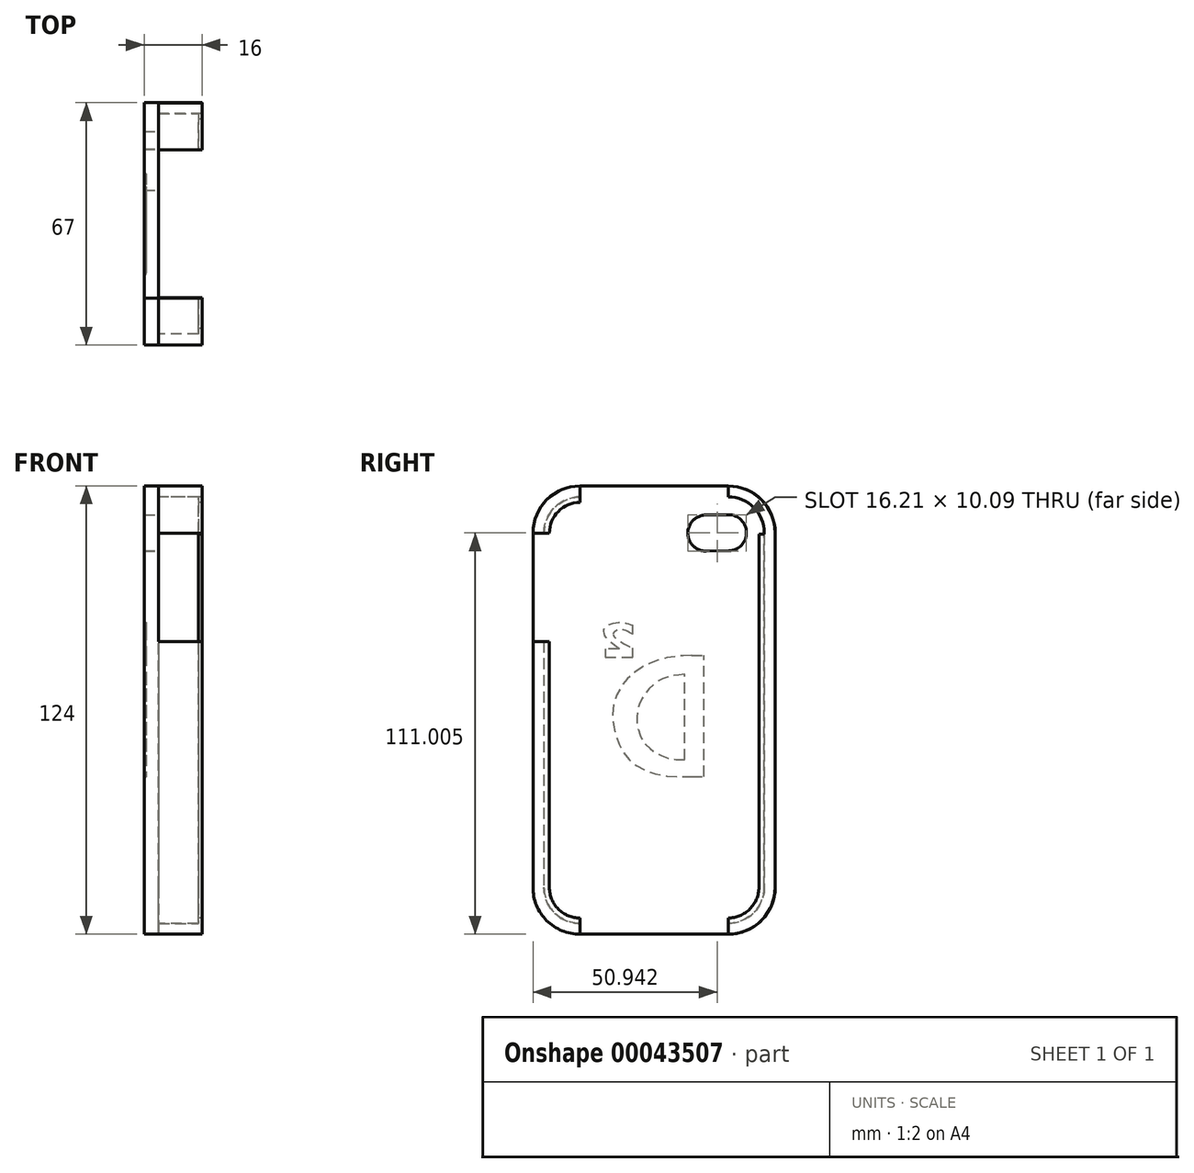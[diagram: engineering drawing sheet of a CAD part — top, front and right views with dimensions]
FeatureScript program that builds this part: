
annotation { "Feature Type Name" : "Feature", "Feature Type Description" : "" }
export const myFeature = defineFeature(function(context is Context, id is Id, definition is map)
    precondition{}
    {
        {
            var Q0;
            Q0=qCreatedBy(makeId("Right.planeOp"),FACE);
            var sketch = newSketch(context, id + "F0", { "sketchPlane" : qUnion([Q0])});
            skLineSegment(sketch, "E0.rect.bottom", {"start": v(20.5, 62) * mm, "end": v(-20.5, 62) * mm});
            skLineSegment(sketch, "E0.rect.top", {"start": v(20.5, -62) * mm, "end": v(-20.5, -62) * mm});
            skLineSegment(sketch, "E0.rect.left", {"start": v(33.5, 49) * mm, "end": v(33.5, -49) * mm});
            skLineSegment(sketch, "E0.rect.right", {"start": v(-33.5, 49) * mm, "end": v(-33.5, -49) * mm});
            skPoint(sketch, "E0.rect.middle", {"position": v(0, 0) * mm});
            skPoint(sketch, "E1.visualSharp", {"position": v(-33.5, 62) * mm});
            skArc(sketch, "E1.filletArc", {"start": v(-20.5, 62) * mm, "mid": v(-29.7, 58.2) * mm, "end": v(-33.5, 49) * mm});
            skPoint(sketch, "E2.visualSharp", {"position": v(-33.5, -62) * mm});
            skArc(sketch, "E2.filletArc", {"start": v(-33.5, -49) * mm, "mid": v(-29.7, -58.2) * mm, "end": v(-20.5, -62) * mm});
            skPoint(sketch, "E3.visualSharp", {"position": v(33.5, 62) * mm});
            skArc(sketch, "E3.filletArc", {"start": v(33.5, 49) * mm, "mid": v(29.7, 58.2) * mm, "end": v(20.5, 62) * mm});
            skPoint(sketch, "E4.visualSharp", {"position": v(33.5, -62) * mm});
            skArc(sketch, "E4.filletArc", {"start": v(20.5, -62) * mm, "mid": v(29.7, -58.2) * mm, "end": v(33.5, -49) * mm});
            skSolve(sketch);
        }
        {
            var Q0;
            Q0 = qSketchRegion(id + "F0", true);
            extrude(context, id + "F1", {"entities" : qUnion([Q0]), "depth" : 4 * mm});
        }
        {
            var Q0;
            Q0=qCreatedBy(makeId("Right.planeOp"),FACE);
            var sketch = newSketch(context, id + "F2", { "sketchPlane" : qUnion([Q0])});
            skArc(sketch, "E5", {"start": v(20.7, 44.05) * mm, "mid": v(25.55, 49.12) * mm, "end": v(20.55, 54.05) * mm});
            skLineSegment(sketch, "E6", {"start": v(20.55, 54.05) * mm, "end": v(14.26, 53.96) * mm});
            skLineSegment(sketch, "E7", {"start": v(20.7, 44.05) * mm, "end": v(14.4, 43.96) * mm});
            skArc(sketch, "E8", {"start": v(14.26, 53.96) * mm, "mid": v(9.34, 48.89) * mm, "end": v(14.4, 43.96) * mm});
            skLineSegment(sketch, "E9", {"start": v(14.26, 53.96) * mm, "end": v(14.4, 43.96) * mm, "construction": true});
            skLineSegment(sketch, "E10", {"start": v(20.55, 54.05) * mm, "end": v(20.7, 44.05) * mm, "construction": true});
            skSolve(sketch);
        }
        {
            var Q0;
            Q0=makeQuery(id+"F2.imprint","IMPRINT",FACE,{"disambiguationData":[TD([[makeQuery(id+"F2.imprint","IMPRINT",EDGE,{"derivedFrom":sQuery(id+"F2.wireOp",EDGE,"E5")}),1.0]])]});
            extrude(context, id + "F3", {"entities" : qUnion([Q0]), "operationType" : NewBodyOperationType.REMOVE, "oppositeDirection" : true, "depth" : 25.4 * mm, "hasSecondDirection" : true, "secondDirectionOppositeDirection" : false, "secondDirectionDepth" : 33.72 * mm});
        }
        {
            var Q0;
            Q0=qCreatedBy(makeId("Right.planeOp"),FACE);
            var sketch = newSketch(context, id + "F4", { "sketchPlane" : qUnion([Q0])});
            skLineSegment(sketch, "E11.bottom", {"start": v(13.8, 15.16) * mm, "end": v(10.36, 15.16) * mm});
            skLineSegment(sketch, "E11.top", {"start": v(13.8, -18.37) * mm, "end": v(10.36, -18.37) * mm});
            skLineSegment(sketch, "E11.left", {"start": v(13.8, 15.16) * mm, "end": v(13.8, -18.37) * mm});
            skFitSpline(sketch, "E12", {"points": [v(10.36, 15.16) * mm, v(2.8, 14.3) * mm, v(-5.23, 10.55) * mm, v(-10.98, 2.35) * mm, v(-10.02, -8.63) * mm, v(-3.92, -15.96) * mm, v(10.36, -18.37) * mm], "startDerivative": vector(-52.68, -2.78) * mm, "endDerivative": vector(80, 5.61) * mm});
            skLineSegment(sketch, "E13", {"start": v(8.44, 9.88) * mm, "end": v(8.44, -13.75) * mm});
            skFitSpline(sketch, "E14", {"points": [v(8.44, 9.88) * mm, v(3.13, 8.92) * mm, v(-1.4, 5.87) * mm, v(-4.55, 0) * mm, v(-4.02, -6.6) * mm, v(-0.62, -11.04) * mm, v(8.44, -13.75) * mm], "startDerivative": vector(-36.15, -4.17) * mm, "endDerivative": vector(56.67, 3.08) * mm});
            skLineSegment(sketch, "E15", {"start": v(-5.94, 23.49) * mm, "end": v(-5.94, 20.96) * mm});
            skFitSpline(sketch, "E16", {"points": [v(-5.94, 20.96) * mm, v(-9.35, 22.28) * mm, v(-11.32, 20.96) * mm, v(-5.94, 17.12) * mm], "startDerivative": vector(-10.5, 6.63) * mm, "endDerivative": vector(19.02, -9.58) * mm});
            skLineSegment(sketch, "E17", {"start": v(-5.94, 17.12) * mm, "end": v(-5.94, 14.6) * mm});
            skLineSegment(sketch, "E18", {"start": v(-5.94, 14.6) * mm, "end": v(-13.52, 14.6) * mm});
            skLineSegment(sketch, "E19", {"start": v(-13.52, 14.6) * mm, "end": v(-13.52, 16.9) * mm});
            skLineSegment(sketch, "E20", {"start": v(-13.52, 16.9) * mm, "end": v(-9.57, 16.9) * mm});
            skFitSpline(sketch, "E21", {"points": [v(-9.57, 16.9) * mm, v(-13.52, 20.52) * mm, v(-13.52, 22.94) * mm, v(-9.57, 24.26) * mm, v(-5.94, 23.49) * mm], "startDerivative": vector(-16.46, 11.92) * mm, "endDerivative": vector(13.67, -4.73) * mm});
            skSolve(sketch);
        }
        {
            var Q0;
            Q0 = qSketchRegion(id + "F4", true);
            extrude(context, id + "F5", {"entities" : qUnion([Q0]), "operationType" : NewBodyOperationType.REMOVE, "depth" : 0.5 * mm, "hasSecondDirection" : true, "secondDirectionOppositeDirection" : true, "secondDirectionDepth" : 10 * mm});
        }
        {
            var Q0;
            Q0=qCreatedBy(makeId("Right.planeOp"),FACE);
            var sketch = newSketch(context, id + "F6", { "sketchPlane" : qUnion([Q0])});
            skLineSegment(sketch, "E22", {"start": v(-30.46, 18.92) * mm, "end": v(-33.5, 18.92) * mm});
            skLineSegment(sketch, "E23", {"start": v(-33.5, 18.92) * mm, "end": v(-33.5, -49) * mm});
            skLineSegment(sketch, "E24", {"start": v(-33.5, -49) * mm, "end": v(-30.46, -49) * mm});
            skLineSegment(sketch, "E25", {"start": v(-30.46, -49) * mm, "end": v(-30.46, 18.92) * mm});
            skSolve(sketch);
        }
        {
            var Q0;
            Q0 = qSketchRegion(id + "F6", true);
            extrude(context, id + "F7", {"entities" : qUnion([Q0]), "operationType" : NewBodyOperationType.ADD, "depth" : 16 * mm});
        }
        {
            var Q0;
            Q0=qCreatedBy(makeId("Right.planeOp"),FACE);
            var sketch = newSketch(context, id + "F8", { "sketchPlane" : qUnion([Q0])});
            skLineSegment(sketch, "E26", {"start": v(-33.5, -49) * mm, "end": v(-30.46, -49) * mm});
            skLineSegment(sketch, "E27", {"start": v(-20.5, -59) * mm, "end": v(-20.5, -62) * mm});
            skArc(sketch, "E28", {"start": v(-30.46, -49) * mm, "mid": v(-27.56, -56.07) * mm, "end": v(-20.5, -59) * mm});
            skArc(sketch, "E29", {"start": v(-33.5, -49) * mm, "mid": v(-29.7, -58.2) * mm, "end": v(-20.5, -62) * mm});
            skSolve(sketch);
        }
        {
            var Q0;
            Q0 = qSketchRegion(id + "F8", true);
            extrude(context, id + "F9", {"entities" : qUnion([Q0]), "operationType" : NewBodyOperationType.ADD, "depth" : 16 * mm});
        }
        {
            var Q0;
            Q0=qCreatedBy(makeId("Right.planeOp"),FACE);
            var sketch = newSketch(context, id + "F10", { "sketchPlane" : qUnion([Q0])});
            skLineSegment(sketch, "E30", {"start": v(-30.47, 48.93) * mm, "end": v(-33.5, 48.93) * mm});
            skLineSegment(sketch, "E31", {"start": v(-20.5, 62) * mm, "end": v(-20.5, 58.97) * mm});
            skArc(sketch, "E32", {"start": v(-20.5, 58.97) * mm, "mid": v(-27.55, 56) * mm, "end": v(-30.47, 48.93) * mm});
            skArc(sketch, "E33", {"start": v(-20.5, 62) * mm, "mid": v(-29.7, 58.15) * mm, "end": v(-33.5, 48.93) * mm});
            skSolve(sketch);
        }
        {
            var Q0;
            Q0 = qSketchRegion(id + "F10", true);
            extrude(context, id + "F11", {"entities" : qUnion([Q0]), "operationType" : NewBodyOperationType.ADD, "depth" : 16 * mm});
        }
        {
            var Q0;
            Q0=qCreatedBy(makeId("Right.planeOp"),FACE);
            var sketch = newSketch(context, id + "F12", { "sketchPlane" : qUnion([Q0])});
            skLineSegment(sketch, "E34", {"start": v(20.49, -62) * mm, "end": v(20.49, -59) * mm});
            skLineSegment(sketch, "E35", {"start": v(33.5, -49) * mm, "end": v(30.5, -49) * mm});
            skArc(sketch, "E36", {"start": v(20.49, -59) * mm, "mid": v(27.55, -56.06) * mm, "end": v(30.5, -49) * mm});
            skArc(sketch, "E37", {"start": v(20.49, -62) * mm, "mid": v(29.67, -58.19) * mm, "end": v(33.5, -49) * mm});
            skSolve(sketch);
        }
        {
            var Q0;
            Q0 = qSketchRegion(id + "F12", true);
            extrude(context, id + "F13", {"entities" : qUnion([Q0]), "operationType" : NewBodyOperationType.ADD, "depth" : 16 * mm});
        }
        {
            var Q0;
            Q0=qCreatedBy(makeId("Right.planeOp"),FACE);
            var sketch = newSketch(context, id + "F14", { "sketchPlane" : qUnion([Q0])});
            skLineSegment(sketch, "E38", {"start": v(33.46, 49) * mm, "end": v(30.5, 49) * mm});
            skLineSegment(sketch, "E39", {"start": v(20.5, 62) * mm, "end": v(20.5, 58.99) * mm});
            skArc(sketch, "E40", {"start": v(33.46, 49) * mm, "mid": v(29.66, 58.17) * mm, "end": v(20.5, 62) * mm});
            skArc(sketch, "E41", {"start": v(30.5, 49) * mm, "mid": v(27.55, 56.05) * mm, "end": v(20.5, 58.99) * mm});
            skSolve(sketch);
        }
        {
            var Q0;
            Q0 = qSketchRegion(id + "F14", true);
            extrude(context, id + "F15", {"entities" : qUnion([Q0]), "operationType" : NewBodyOperationType.ADD, "depth" : 16 * mm});
        }
        {
            var Q0;
            Q0=qCreatedBy(makeId("Right.planeOp"),FACE);
            var sketch = newSketch(context, id + "F16", { "sketchPlane" : qUnion([Q0])});
            skLineSegment(sketch, "E42", {"start": v(30.5, -49) * mm, "end": v(33.49, -49) * mm});
            skLineSegment(sketch, "E43", {"start": v(33.49, -49) * mm, "end": v(33.49, 49) * mm});
            skLineSegment(sketch, "E44", {"start": v(33.49, 49) * mm, "end": v(30.5, 49) * mm});
            skLineSegment(sketch, "E45", {"start": v(30.5, 49) * mm, "end": v(30.5, -49) * mm});
            skSolve(sketch);
        }
        {
            var Q0;
            Q0 = qSketchRegion(id + "F16", true);
            extrude(context, id + "F17", {"entities" : qUnion([Q0]), "operationType" : NewBodyOperationType.ADD, "depth" : 16 * mm});
        }
        {
            var Q0;
            Q0=qCreatedBy(makeId("Right.planeOp"),FACE);
            var sketch = newSketch(context, id + "F18", { "sketchPlane" : qUnion([Q0])});
            skLineSegment(sketch, "E46", {"start": v(-30.46, 18.92) * mm, "end": v(-30.46, -49.07) * mm});
            skLineSegment(sketch, "E47", {"start": v(-30.46, -49.07) * mm, "end": v(-28.96, -49.07) * mm});
            skLineSegment(sketch, "E48", {"start": v(-28.96, -49.07) * mm, "end": v(-28.96, 18.92) * mm});
            skLineSegment(sketch, "E49", {"start": v(-28.96, 18.92) * mm, "end": v(-30.46, 18.92) * mm});
            skLineSegment(sketch, "E50", {"start": v(-20.5, -59) * mm, "end": v(-20.5, -57.5) * mm});
            skArc(sketch, "E51", {"start": v(-30.46, -49.07) * mm, "mid": v(-27.53, -56.1) * mm, "end": v(-20.5, -59) * mm});
            skArc(sketch, "E52", {"start": v(-28.96, -49.07) * mm, "mid": v(-26.47, -55.04) * mm, "end": v(-20.5, -57.5) * mm});
            skLineSegment(sketch, "E53", {"start": v(-30.47, 48.93) * mm, "end": v(-28.97, 48.93) * mm});
            skLineSegment(sketch, "E54", {"start": v(-20.5, 58.97) * mm, "end": v(-20.5, 57.47) * mm});
            skArc(sketch, "E55", {"start": v(-20.5, 58.97) * mm, "mid": v(-27.55, 56) * mm, "end": v(-30.47, 48.93) * mm});
            skArc(sketch, "E56", {"start": v(-20.5, 57.47) * mm, "mid": v(-26.5, 54.95) * mm, "end": v(-28.97, 48.93) * mm});
            skLineSegment(sketch, "E57", {"start": v(30.5, 48.62) * mm, "end": v(29, 48.62) * mm});
            skLineSegment(sketch, "E58", {"start": v(30.5, -49) * mm, "end": v(29, -49) * mm});
            skLineSegment(sketch, "E59", {"start": v(29, -49) * mm, "end": v(29, 48.62) * mm});
            skLineSegment(sketch, "E60", {"start": v(30.5, 48.62) * mm, "end": v(30.5, -49) * mm});
            skLineSegment(sketch, "E61", {"start": v(20.49, -59) * mm, "end": v(20.49, -57.5) * mm});
            skArc(sketch, "E62", {"start": v(20.49, -59) * mm, "mid": v(27.54, -56.06) * mm, "end": v(30.5, -49) * mm});
            skArc(sketch, "E63", {"start": v(20.49, -57.5) * mm, "mid": v(26.5, -55.02) * mm, "end": v(29, -49) * mm});
            skSolve(sketch);
        }
        {
            var Q0;
            Q0 = qSketchRegion(id + "F18", true);
            extrude(context, id + "F19", {"entities" : qUnion([Q0]), "operationType" : NewBodyOperationType.ADD, "depth" : 16 * mm, "hasSecondDirection" : true, "secondDirectionOppositeDirection" : false, "secondDirectionDepth" : 15 * mm});
        }
    });
